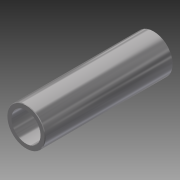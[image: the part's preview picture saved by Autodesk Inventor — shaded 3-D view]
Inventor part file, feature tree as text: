
AUTODESK INVENTOR PART (.ipt)
format: ipt  version: 2016 SP1 (Build 200210100, 210)  size: 113,152 bytes
history: native  units: in
note: dims shown in document units (in); Inventor stores cm internally (conversion verified against a paired STEP export)
features: other x21, revolve x1, sketch x1
ambient origin geometry x8: Origin, YZ Plane, XZ Plane, XY Plane, X Axis, Y Axis, Z Axis, Center Point
bodies: Solid1 (feature_tree)
feature tree (23):
  revolve  "Revolution1"  [1 undecoded]
  other  "cap_XY"
  other  "cap_YZ"
  other  "cap_ZX"
  other  "cap_X"
  other  "cap_Y"
  other  "cap_Z"
  other  "cap_Center"
  other  "ctr_XY"
  other  "ctr_YZ"
  other  "ctr_ZX"
  other  "ctr_X"
  other  "ctr_Y"
  other  "ctr_Z"
  other  "ctr_Center"
  other  "hd_XY"
  other  "hd_YZ"
  other  "hd_ZX"
  other  "hd_X"
  other  "hd_Y"
  other  "hd_Z"
  other  "hd_Center"
  sketch  "Sketch_2"  dims[d0=360.0deg d1=0.0in d2=0.0in]
note: 1 required parameter value undecoded (feature->parameter linkage not recoverable at this tier; creation-order binding heuristic only, values carry confidence <= 0.55)
